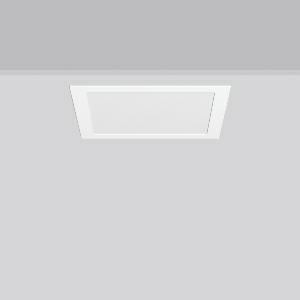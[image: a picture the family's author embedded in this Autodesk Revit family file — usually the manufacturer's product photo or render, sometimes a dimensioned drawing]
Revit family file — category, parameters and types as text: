
# Revit family: toledo_flat_square_e_901488_002_1_7dd1
name_source: partatom
category: Lighting Fixtures
units: mm (PartAtom-declared; Revit-internal decimal feet)

## family parameters
Cut with Voids When Loaded = No
Host = Face
Light Source = No
Part Type = Normal
Room Calculation Point = No
Round Connector Dimension = Use Diameter
Shared = No

## types (1)
- TOLEDO FLAT square E (1 x LED Modul 840, 2250 lm, 4000)
    Apparent Load = 21 VA
    CIE Flux Codes = 49 80 96 100 100
    Color Rendering = 80
    Color Temperature = 4000
    Default Elevation = 1800 mm
    Description = Series: TOLEDO FLAT square
Ultra thin recessed downlight. Housing: die-cast aluminium. Light guide and diffuser made of non-yellowing PMMA, opal matt. Ceiling installation with spring system. Mounting depth depends on ceiling strength. Suitable for through-wiring with separately available accessories. Surface mounted housing as accessory for all sizes. Retrofittable decorative cylinders made of chintz fabric as accessory, optional with satin finish plastic diffuser. Through-wiring box (5 pole) available as accessory. 
Colour: white
Length: 300 mm
Width: 300 mm
Height: 3 mm
Cut-out length: 280 mm
Cut-out width: 280 mm
Recess height: 31-56 mm
Luminaire: recess height: 31-51 mm
Lamp: LED
Socket: without socket
Colour temperature: 4000K
Colour rendering index (CRI): 80
System power: 21 W
Rated luminous flux: 2250 lm
Luminous efficiency: 107 lm/W
Control gear: Regulated power supply
Protection class: II
Type of protection: IP 54
    Height = 0 mm  [stored 0 ft]
    Lamp = 1 x LED Modul 840
    Lamp Light Flux = 2250 lm
    Lamp count = 1
    Length = 300 mm
    Lifetime = 50000 h
    Luminous efficacy = 107 lm/W
    Manufacturer = RZB
    ModVariant = No
    Model = 901488.002.1
    Mounting Place = Ceiling
    Mounting Type = Recessed
    Number of Poles = 1
    OnlyDefault = Yes
    Power Factor = 1
    Product Name = TOLEDO FLAT square E
    Product group = Recessed downlights
    ProductGroupID = 402
    Protection Class = Protection class II
    Protection Degree = IP 20
    RLX_Detail_Level = 1
    RLX_Emergency_Light_Flux = 0 lm
    RLX_Emergency_Type = 0
    RLX_Emergency_Type_DB = No
    RlxData = <blob elided: 60949 chars, md5=db29788e>
    Socket = socket
    Standby Power = 0 W
    System Light Flux = 2250 lm
    System Power = 21 W
    Type Comments = Product without accessories
    Type Image = 901488.002.jpg
    URL = http://relux.com
    VarID = ---
    Voltage = 230 V
    Voltage Range = 220-240 V
    Weight = 0.00 kg
    Width = 300 mm

note: [stored X ft] marks values corroborated as IEEE doubles in the binary element streams (Revit-internal decimal feet)

## geometry (parser evidence)
native form markers: Blend x4, Sweep x12
no freeform markers — native parametric forms only
